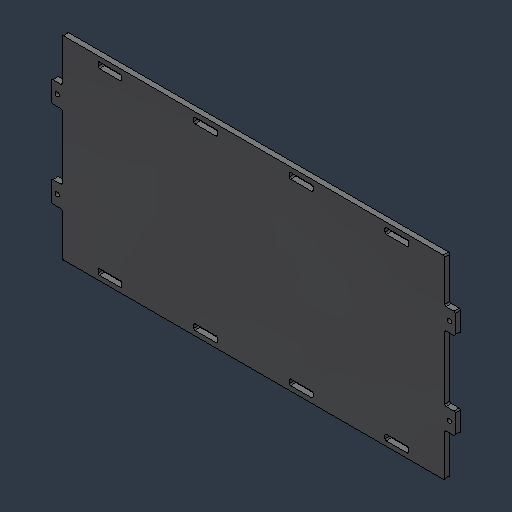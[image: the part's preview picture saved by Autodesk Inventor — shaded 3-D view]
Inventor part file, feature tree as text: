
AUTODESK INVENTOR PART (.ipt)
format: ipt  version: 2024.3 (Build 283343000, 343)  size: 158,720 bytes
history: native  units: mm (DEFAULTED — no unit token found)
features: fillet x1
ambient origin geometry x8: Origin, YZ Plane, XZ Plane, XY Plane, X Axis, Y Axis, Z Axis, Center Point
bodies: Solid1 (feature_tree)
feature tree (1):
  fillet  "Fillet3"  [1 undecoded]
note: 1 required parameter value undecoded (feature->parameter linkage not recoverable at this tier; creation-order binding heuristic only, values carry confidence <= 0.55)
